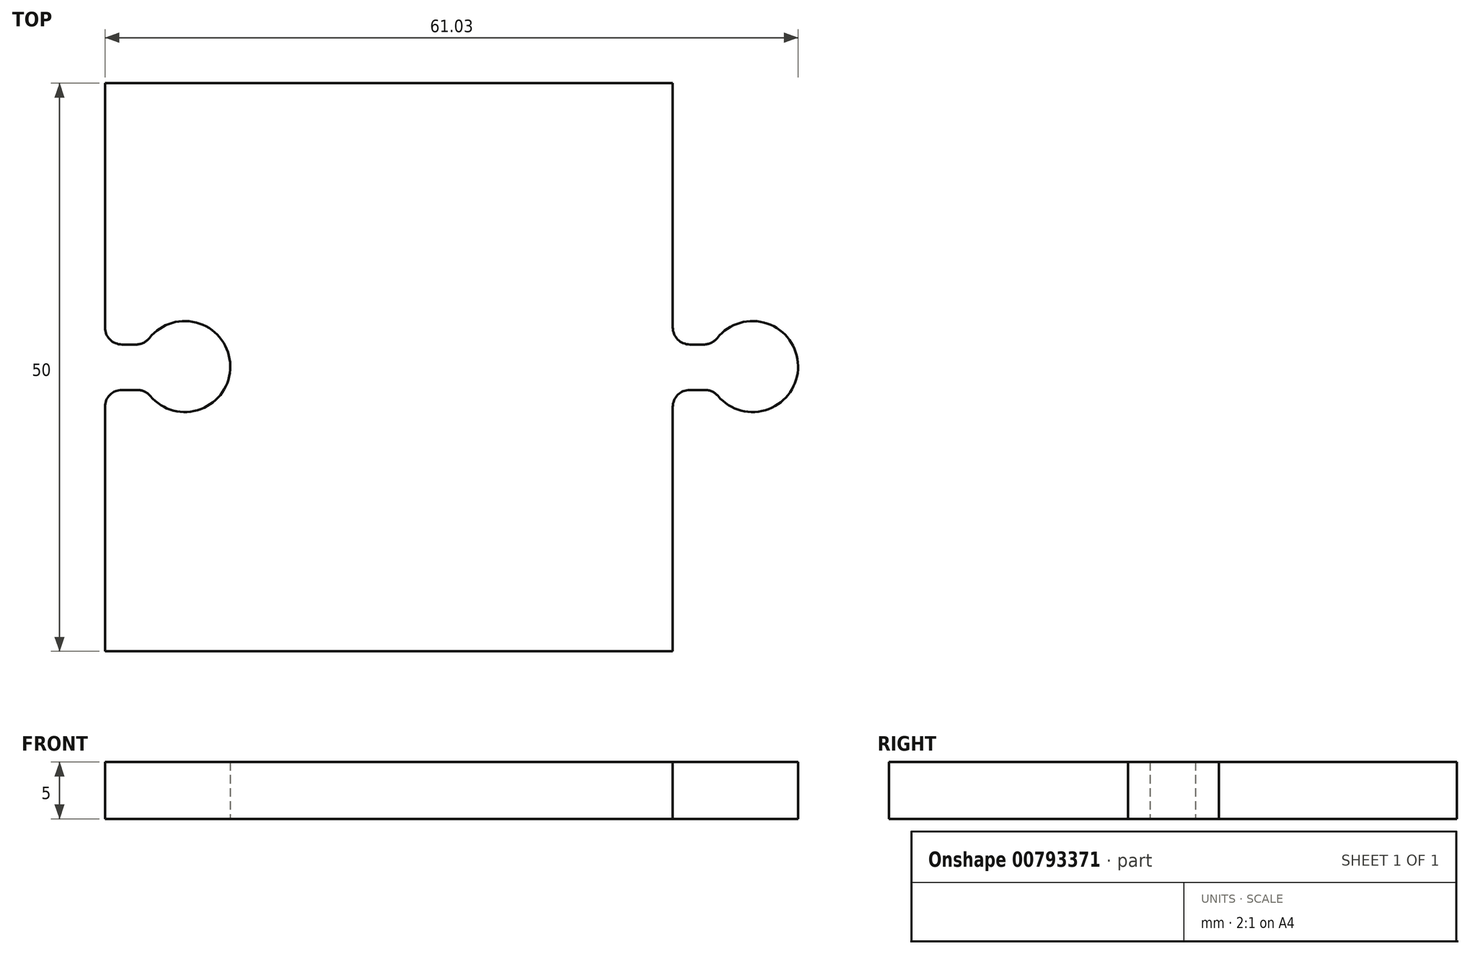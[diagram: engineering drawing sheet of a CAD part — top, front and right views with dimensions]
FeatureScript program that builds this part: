
annotation { "Feature Type Name" : "Feature", "Feature Type Description" : "" }
export const myFeature = defineFeature(function(context is Context, id is Id, definition is map)
    precondition{}
    {
        {
            var Q0;
            Q0=qCreatedBy(makeId("Top.planeOp"),FACE);
            var sketch = newSketch(context, id + "F0", { "sketchPlane" : qUnion([Q0])});
            skLineSegment(sketch, "E0.bottom", {"start": v(0, 0) * mm, "end": v(-50, 0) * mm});
            skLineSegment(sketch, "E0.top", {"start": v(0, 50) * mm, "end": v(-50, 50) * mm});
            skLineSegment(sketch, "E0.left", {"start": v(0, 0) * mm, "end": v(0, 21.5) * mm});
            skLineSegment(sketch, "E0.right", {"start": v(-50, 0) * mm, "end": v(-50, 21.5) * mm});
            skLineSegment(sketch, "E1", {"start": v(-48.5, 23) * mm, "end": v(-47.16, 23) * mm});
            skLineSegment(sketch, "E2", {"start": v(-50, 50) * mm, "end": v(-50, 28.5) * mm});
            skLineSegment(sketch, "E3", {"start": v(-48.5, 27) * mm, "end": v(-47.26, 27) * mm});
            skArc(sketch, "E4", {"start": v(-46.02, 22.47) * mm, "mid": v(-38.97, 25.11) * mm, "end": v(-46.09, 27.56) * mm});
            skPoint(sketch, "E5.end.orphan", {"position": v(-50, 25) * mm});
            skLineSegment(sketch, "E6.trimOffspring", {"start": v(-50, 28.5) * mm, "end": v(-50, 50) * mm});
            skPoint(sketch, "E7.visualSharp", {"position": v(-50, 27) * mm});
            skArc(sketch, "E7.filletArc", {"start": v(-50, 28.5) * mm, "mid": v(-49.56, 27.44) * mm, "end": v(-48.5, 27) * mm});
            skPoint(sketch, "E8.visualSharp", {"position": v(-50, 23) * mm});
            skArc(sketch, "E8.filletArc", {"start": v(-48.5, 23) * mm, "mid": v(-49.56, 22.56) * mm, "end": v(-50, 21.5) * mm});
            skPoint(sketch, "E9.visualSharp", {"position": v(-46.46, 27) * mm});
            skArc(sketch, "E9.filletArc", {"start": v(-47.26, 27) * mm, "mid": v(-46.6, 27.15) * mm, "end": v(-46.09, 27.56) * mm});
            skPoint(sketch, "E10.visualSharp", {"position": v(-46.4, 23) * mm});
            skArc(sketch, "E10.filletArc", {"start": v(-46.02, 22.47) * mm, "mid": v(-46.53, 22.86) * mm, "end": v(-47.16, 23) * mm});
            skLineSegment(sketch, "E11", {"start": v(-42.97, 25.06) * mm, "end": v(-50, 25) * mm});
            skPoint(sketch, "E12.orphan", {"position": v(0, 25.06) * mm});
            skLineSegment(sketch, "E13", {"start": v(0, 50) * mm, "end": v(0, 28.5) * mm});
            skLineSegment(sketch, "E14", {"start": v(1.5, 23) * mm, "end": v(2.83, 23) * mm});
            skLineSegment(sketch, "E15", {"start": v(1.5, 27) * mm, "end": v(2.74, 27) * mm});
            skArc(sketch, "E16", {"start": v(3.98, 22.47) * mm, "mid": v(11.03, 25.11) * mm, "end": v(3.9, 27.56) * mm});
            skPoint(sketch, "E17.visualSharp", {"position": v(0, 27) * mm});
            skArc(sketch, "E17.filletArc", {"start": v(0, 28.5) * mm, "mid": v(0.44, 27.44) * mm, "end": v(1.5, 27) * mm});
            skPoint(sketch, "E18.newPointA", {"position": v(0, 23) * mm});
            skArc(sketch, "E18.filletArc", {"start": v(1.5, 23) * mm, "mid": v(0.44, 22.56) * mm, "end": v(0, 21.5) * mm});
            skPoint(sketch, "E19.orphan", {"position": v(10.46, 27) * mm});
            skLineSegment(sketch, "E20.trimOffspring", {"start": v(10.46, 23) * mm, "end": v(10.46, 23) * mm});
            skPoint(sketch, "E21.visualSharp", {"position": v(3.53, 27) * mm});
            skArc(sketch, "E21.filletArc", {"start": v(2.74, 27) * mm, "mid": v(3.39, 27.15) * mm, "end": v(3.9, 27.56) * mm});
            skPoint(sketch, "E22.visualSharp", {"position": v(3.6, 23) * mm});
            skArc(sketch, "E22.filletArc", {"start": v(3.98, 22.47) * mm, "mid": v(3.46, 22.86) * mm, "end": v(2.83, 23) * mm});
            skSolve(sketch);
        }
        {
            var Q0;
            Q0 = qSketchRegion(id + "F0", true);
            extrude(context, id + "F1", {"entities" : qUnion([Q0]), "depth" : 5 * mm, "offsetDistance" : 25 * mm});
        }
    });
